# Revit family: FP-Revit20-en-VB30SDB1-VB30SDX1-VacuumDrawer-0-9000XXXX-US-CA
name_source: partatom
category: Generic Models
units: mm (PartAtom-declared; Revit-internal decimal feet)

## family parameters
Always vertical = Yes
Can host rebar = No
Cut with Voids When Loaded = No
Part Type = Normal
Room Calculation Point = No
Round Connector Dimension = Use Diameter
Shared = No
Work Plane-Based = No

## types (2) — shared parameters
Cavity - Minimum Depth = 580 mm  [stored 1.90289 ft]
Cavity - Minimum Height = 273 mm  [stored 0.895669 ft]
Cavity - Minimum width = 724 mm  [stored 2.37533 ft]
Chassis - Depth = 546 mm  [stored 1.79134 ft]
Chassis - Depth (including power plug, excluding flange) = 551 mm  [stored 1.80774 ft]
Chassis - width = 722 mm  [stored 2.36877 ft]
Connector note electrical = 120 v, 60 Hz, 10 A
Description = Vacuum Drawer, 30"
Manufacturer = Fisher & Paykel Appliances
Material - Chassis = Fisher & Paykel - Aluminium
Overall Depth - (Including front panel & power plug) = 571 mm  [stored 1.87336 ft]
Product - Overall Height = 271 mm  [stored 0.889108 ft]
Product - Overall width = 760 mm
URL = www.fisherpaykel.com
zero-valued in all types: Default Elevation

## per-type parameters (varying)
| type | Material - Glass |
| VB30SDB1 | Fisher & Paykel - Glass, Black |
| VB30SDX1 | Fisher & Paykel - Stainless Steel |

note: column(s) folded — value = type name in every type: Model

note: [stored X ft] marks values corroborated as IEEE doubles in the binary element streams (Revit-internal decimal feet)

## geometry (parser evidence)
native form markers: Sweep x2
no freeform markers — native parametric forms only
